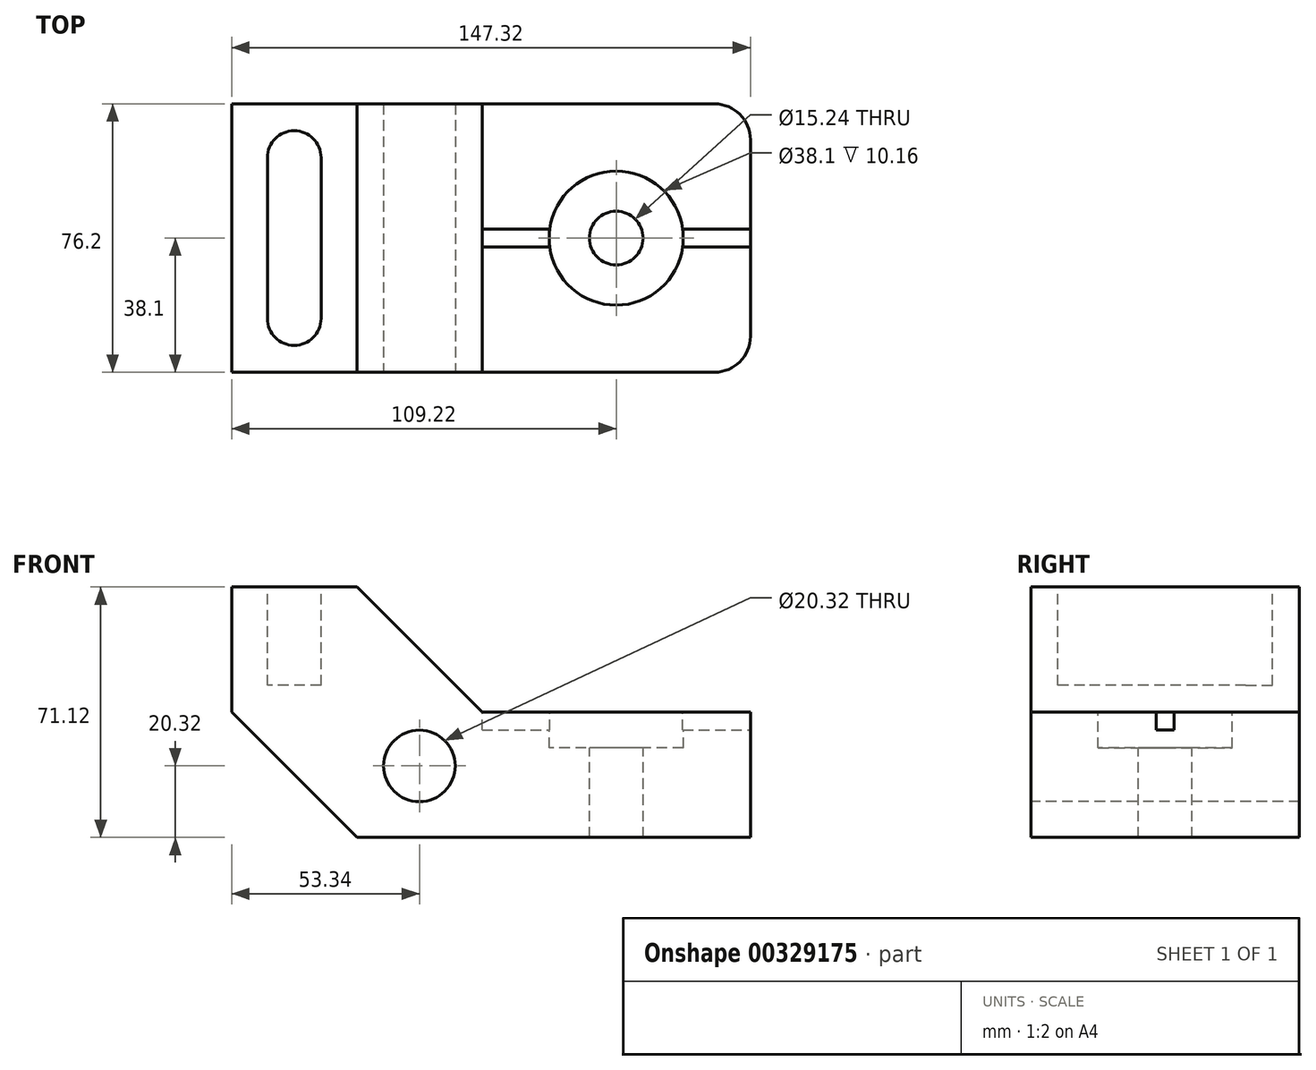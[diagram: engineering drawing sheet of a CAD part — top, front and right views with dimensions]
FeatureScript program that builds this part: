
annotation { "Feature Type Name" : "Feature", "Feature Type Description" : "" }
export const myFeature = defineFeature(function(context is Context, id is Id, definition is map)
    precondition{}
    {
        {
            var Q0;
            Q0=qCreatedBy(makeId("Front.planeOp"),FACE);
            var sketch = newSketch(context, id + "F0", { "sketchPlane" : qUnion([Q0])});
            skLineSegment(sketch, "E0", {"start": v(0, 35.56) * mm, "end": v(0, 71.12) * mm});
            skLineSegment(sketch, "E1", {"start": v(0, 71.12) * mm, "end": v(35.56, 71.12) * mm});
            skLineSegment(sketch, "E2", {"start": v(35.56, 71.12) * mm, "end": v(71.12, 35.56) * mm});
            skLineSegment(sketch, "E3", {"start": v(71.12, 35.56) * mm, "end": v(147.32, 35.56) * mm});
            skLineSegment(sketch, "E4", {"start": v(147.32, 35.56) * mm, "end": v(147.32, 0) * mm});
            skLineSegment(sketch, "E5", {"start": v(147.32, 0) * mm, "end": v(35.56, 0) * mm});
            skLineSegment(sketch, "E6", {"start": v(35.56, 0) * mm, "end": v(0, 35.56) * mm});
            skSolve(sketch);
        }
        {
            var Q0;
            Q0=makeQuery(id+"F0.imprint","IMPRINT",FACE,{"disambiguationData":[TD([[makeQuery(id+"F0.imprint","IMPRINT",EDGE,{"derivedFrom":sQuery(id+"F0.wireOp",EDGE,"E0")}),-1.0]])]});
            extrude(context, id + "F1", {"entities" : qUnion([Q0]), "depth" : 76.2 * mm});
        }
        {
            var Q0;
            Q0=makeQuery(id+"F1.opExtrude","CAP_FACE",FACE,{"disambiguationData":[OSD([sQuery(id+"F0.wireOp",EDGE,"E0"),sQuery(id+"F0.wireOp",EDGE,"E1"),sQuery(id+"F0.wireOp",EDGE,"E2"),sQuery(id+"F0.wireOp",EDGE,"E3"),sQuery(id+"F0.wireOp",EDGE,"E4"),sQuery(id+"F0.wireOp",EDGE,"E5"),sQuery(id+"F0.wireOp",EDGE,"E6")])],"isStart":false});
            var sketch = newSketch(context, id + "F2", { "sketchPlane" : qUnion([Q0])});
            skCircle(sketch, "E7", {"center": v(53.34, 20.32) * mm, "radius": 10.16 * mm});
            skSolve(sketch);
        }
        {
            var Q0;
            Q0=makeQuery(id+"F2.imprint","IMPRINT",FACE,{"disambiguationData":[TD([[makeQuery(id+"F2.imprint","IMPRINT",EDGE,{"derivedFrom":sQuery(id+"F2.wireOp",EDGE,"E7")}),1.0]])]});
            extrude(context, id + "F3", {"entities" : qUnion([Q0]), "operationType" : NewBodyOperationType.REMOVE, "endBound" : BoundingType.THROUGH_ALL, "oppositeDirection" : true, "depth" : 25.4 * mm});
        }
        {
            var Q0;
            Q0=makeQuery(id+"F1.opExtrude","SWEPT_FACE",FACE,{"disambiguationData":[OSD([sQuery(id+"F0.wireOp",EDGE,"E1")])]});
            var sketch = newSketch(context, id + "F4", { "sketchPlane" : qUnion([Q0])});
            skLineSegment(sketch, "E8", {"start": v(10.16, -15.24) * mm, "end": v(10.16, -60.96) * mm});
            skLineSegment(sketch, "E9", {"start": v(25.4, -15.24) * mm, "end": v(25.4, -60.96) * mm});
            skArc(sketch, "E10", {"start": v(10.16, -15.24) * mm, "mid": v(17.78, -7.62) * mm, "end": v(25.4, -15.24) * mm});
            skArc(sketch, "E11", {"start": v(10.16, -60.96) * mm, "mid": v(17.78, -68.58) * mm, "end": v(25.4, -60.96) * mm});
            skSolve(sketch);
        }
        {
            var Q0;
            Q0=makeQuery(id+"F4.imprint","IMPRINT",FACE,{"disambiguationData":[TD([[makeQuery(id+"F4.imprint","IMPRINT",EDGE,{"derivedFrom":sQuery(id+"F4.wireOp",EDGE,"E8")}),1.0]])]});
            extrude(context, id + "F5", {"entities" : qUnion([Q0]), "operationType" : NewBodyOperationType.REMOVE, "oppositeDirection" : true, "depth" : 27.94 * mm});
        }
        {
            var Q0;
            Q0=makeQuery(id+"F1.opExtrude","SWEPT_FACE",FACE,{"disambiguationData":[OSD([sQuery(id+"F0.wireOp",EDGE,"E3")])]});
            var sketch = newSketch(context, id + "F6", { "sketchPlane" : qUnion([Q0])});
            skCircle(sketch, "E12", {"center": v(109.22, -38.1) * mm, "radius": 15.24 * mm});
            skSolve(sketch);
        }
        {
            var Q0;
            Q0=sQuery(id+"F6.wireOp",VERTEX,"E12.center");
            var Q1;
            Q1=makeQuery(id+"F1.opExtrude","SWEPT_BODY",BODY,{"disambiguationData":[OSD([sQuery(id+"F0.wireOp",EDGE,"E0"),sQuery(id+"F0.wireOp",EDGE,"E1"),sQuery(id+"F0.wireOp",EDGE,"E2"),sQuery(id+"F0.wireOp",EDGE,"E3"),sQuery(id+"F0.wireOp",EDGE,"E4"),sQuery(id+"F0.wireOp",EDGE,"E5"),sQuery(id+"F0.wireOp",EDGE,"E6")])]});
            hole(context, id + "F7", {"style" : HoleStyle.C_BORE, "endStyle" : HoleEndStyle.THROUGH, "holeDiameter" : 15.24 * mm, "cBoreDiameter" : 38.1 * mm, "cBoreDepth" : 10.16 * mm, "tappedDepth" : 12.7 * mm, "tapClearance" : 3, "startFromSketch" : true, "locations" : qUnion([Q0]), "scope" : qUnion([Q1])});
        }
        {
            var Q0;
            Q0=makeQuery(id+"F1.opExtrude","SWEPT_FACE",FACE,{"disambiguationData":[OSD([sQuery(id+"F0.wireOp",EDGE,"E4")])]});
            var sketch = newSketch(context, id + "F8", { "sketchPlane" : qUnion([Q0])});
            skLineSegment(sketch, "E13", {"start": v(-38.1, 35.56) * mm, "end": v(-40.64, 35.56) * mm});
            skLineSegment(sketch, "E14", {"start": v(-40.64, 35.56) * mm, "end": v(-40.64, 30.48) * mm});
            skLineSegment(sketch, "E15", {"start": v(-40.64, 30.48) * mm, "end": v(-35.56, 30.48) * mm});
            skLineSegment(sketch, "E16", {"start": v(-35.56, 30.48) * mm, "end": v(-35.56, 35.56) * mm});
            skLineSegment(sketch, "E17", {"start": v(-35.56, 35.56) * mm, "end": v(-38.1, 35.56) * mm});
            skSolve(sketch);
        }
        {
            var Q0;
            Q0=makeQuery(id+"F8.imprint","IMPRINT",FACE,{"disambiguationData":[TD([[makeQuery(id+"F8.imprint","IMPRINT",EDGE,{"derivedFrom":sQuery(id+"F8.wireOp",EDGE,"E13")}),-1.0]])]});
            extrude(context, id + "F9", {"entities" : qUnion([Q0]), "operationType" : NewBodyOperationType.REMOVE, "oppositeDirection" : true, "depth" : 76.2 * mm});
        }
        {
            var Q0;
            Q0=makeQuery(id+"F1.opExtrude","CAP_EDGE",EDGE,{"disambiguationData":[OSD([sQuery(id+"F0.wireOp",EDGE,"E4")])],"isStart":true});
            var Q1;
            Q1=makeQuery(id+"F1.opExtrude","CAP_EDGE",EDGE,{"disambiguationData":[OSD([sQuery(id+"F0.wireOp",EDGE,"E4")])],"isStart":false});
            fillet(context, id + "F10", {"entities" : qUnion([Q0, Q1]), "radius" : 10.16 * mm, "tangentPropagation" : true, "allowEdgeOverflow" : false});
        }
    });
